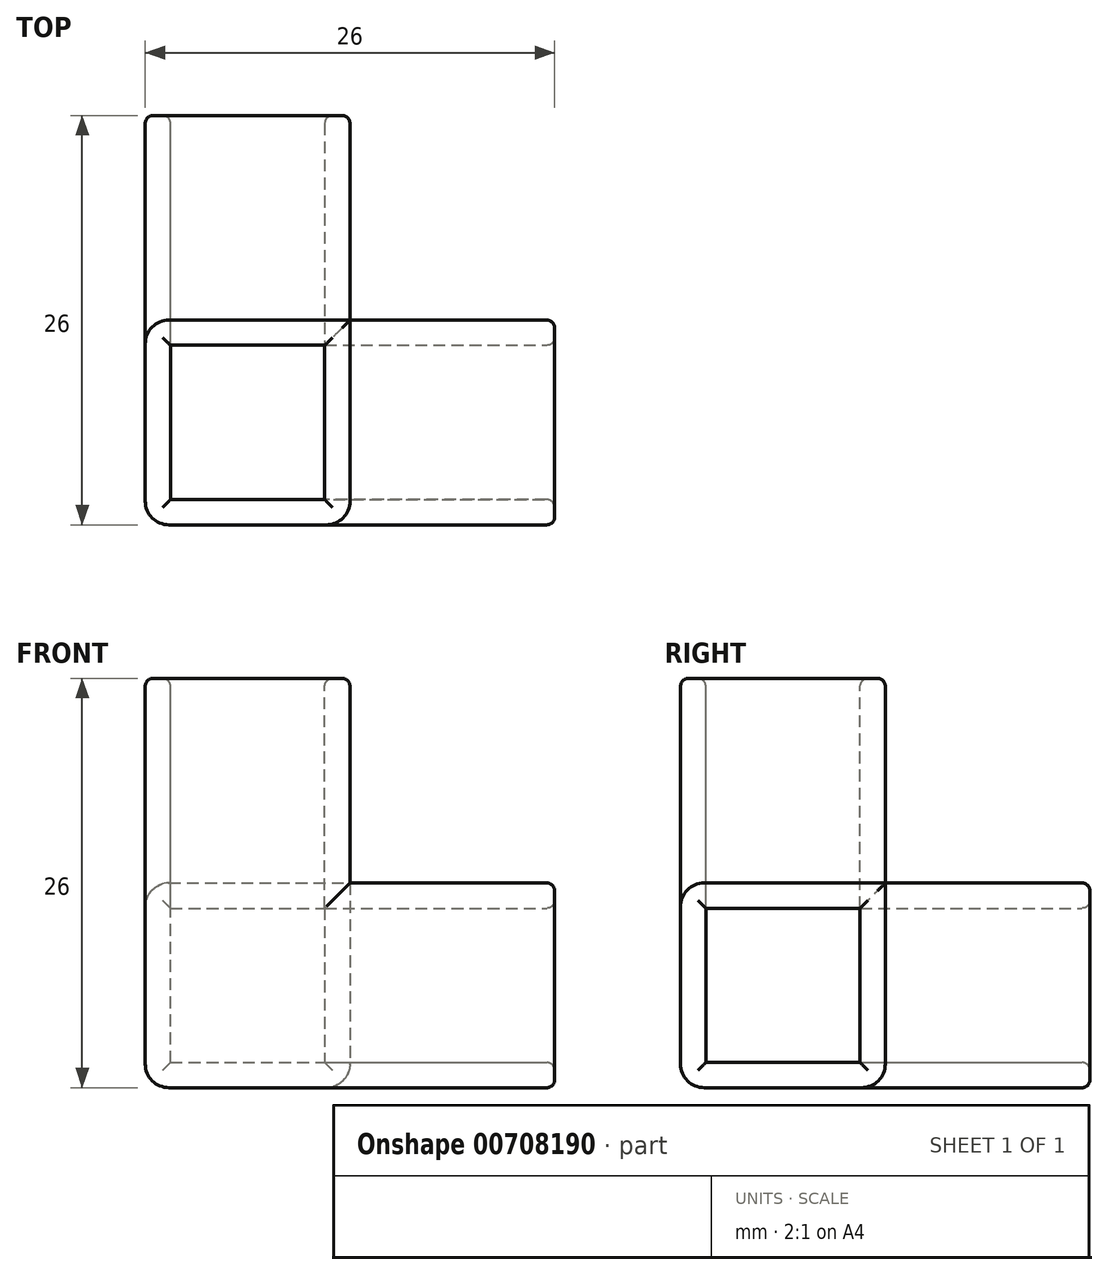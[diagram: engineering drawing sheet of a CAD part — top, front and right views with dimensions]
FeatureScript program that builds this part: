
annotation { "Feature Type Name" : "Feature", "Feature Type Description" : "" }
export const myFeature = defineFeature(function(context is Context, id is Id, definition is map)
    precondition{}
    {
        {
            var Q0;
            Q0=qCreatedBy(makeId("Top.planeOp"),FACE);
            var sketch = newSketch(context, id + "F0", { "sketchPlane" : qUnion([Q0])});
            skLineSegment(sketch, "E0", {"start": v(-6.5, 11.44) * mm, "end": v(-6.5, -1.56) * mm});
            skLineSegment(sketch, "E1", {"start": v(-6.5, -1.56) * mm, "end": v(6.5, -1.56) * mm});
            skLineSegment(sketch, "E2.0", {"start": v(-19.5, -14.56) * mm, "end": v(6.5, -14.56) * mm});
            skLineSegment(sketch, "E2.1", {"start": v(-19.5, 11.44) * mm, "end": v(-19.5, -14.56) * mm});
            skLineSegment(sketch, "E3", {"start": v(-19.5, 11.44) * mm, "end": v(-6.5, 11.44) * mm});
            skLineSegment(sketch, "E4", {"start": v(6.5, -1.56) * mm, "end": v(6.5, -14.56) * mm});
            skSolve(sketch);
        }
        {
            var Q0;
            Q0 = qSketchRegion(id + "F0", true);
            extrude(context, id + "F1", {"entities" : qUnion([Q0]), "depth" : 13 * mm, "offsetDistance" : 25 * mm});
        }
        {
            var Q0;
            Q0=makeQuery(id+"F1.opExtrude","CAP_FACE",FACE,{"disambiguationData":[OSD([sQuery(id+"F0.wireOp",EDGE,"E0"),sQuery(id+"F0.wireOp",EDGE,"E1"),sQuery(id+"F0.wireOp",EDGE,"E2.0"),sQuery(id+"F0.wireOp",EDGE,"E2.1"),sQuery(id+"F0.wireOp",EDGE,"E3"),sQuery(id+"F0.wireOp",EDGE,"E4")])],"isStart":false});
            var sketch = newSketch(context, id + "F2", { "sketchPlane" : qUnion([Q0])});
            skLineSegment(sketch, "E5", {"start": v(-6.5, -1.56) * mm, "end": v(-19.5, -1.56) * mm});
            skLineSegment(sketch, "E6", {"start": v(-19.5, -1.56) * mm, "end": v(-19.5, -14.56) * mm});
            skLineSegment(sketch, "E7", {"start": v(-19.5, -14.56) * mm, "end": v(-6.5, -14.56) * mm});
            skLineSegment(sketch, "E8", {"start": v(-6.5, -14.56) * mm, "end": v(-6.5, -1.56) * mm});
            skSolve(sketch);
        }
        {
            var Q0;
            Q0 = qSketchRegion(id + "F2", true);
            extrude(context, id + "F3", {"entities" : qUnion([Q0]), "operationType" : NewBodyOperationType.ADD, "depth" : 13 * mm, "offsetDistance" : 25 * mm});
        }
        {
            var Q0;
            Q0=makeQuery(id+"F3.opExtrude","CAP_FACE",FACE,{"disambiguationData":[OSD([sQuery(id+"F2.wireOp",EDGE,"E5"),sQuery(id+"F2.wireOp",EDGE,"E6"),sQuery(id+"F2.wireOp",EDGE,"E7"),sQuery(id+"F2.wireOp",EDGE,"E8")])],"isStart":false});
            var sketch = newSketch(context, id + "F4", { "sketchPlane" : qUnion([Q0])});
            skLineSegment(sketch, "E9.bottom", {"start": v(-17.9, -3.16) * mm, "end": v(-8.1, -3.16) * mm});
            skLineSegment(sketch, "E9.top", {"start": v(-17.9, -12.96) * mm, "end": v(-8.1, -12.96) * mm});
            skLineSegment(sketch, "E9.left", {"start": v(-17.9, -3.16) * mm, "end": v(-17.9, -12.96) * mm});
            skLineSegment(sketch, "E9.right", {"start": v(-8.1, -3.16) * mm, "end": v(-8.1, -12.96) * mm});
            skSolve(sketch);
        }
        {
            var Q0;
            Q0=makeQuery(id+"F1.opExtrude","SWEPT_FACE",FACE,{"disambiguationData":[OSD([sQuery(id+"F0.wireOp",EDGE,"E3")])]});
            var sketch = newSketch(context, id + "F5", { "sketchPlane" : qUnion([Q0])});
            skLineSegment(sketch, "E10.bottom", {"start": v(17.9, 1.6) * mm, "end": v(8.1, 1.6) * mm});
            skLineSegment(sketch, "E10.top", {"start": v(17.9, 11.4) * mm, "end": v(8.1, 11.4) * mm});
            skLineSegment(sketch, "E10.left", {"start": v(17.9, 1.6) * mm, "end": v(17.9, 11.4) * mm});
            skLineSegment(sketch, "E10.right", {"start": v(8.1, 1.6) * mm, "end": v(8.1, 11.4) * mm});
            skSolve(sketch);
        }
        {
            var Q0;
            Q0=makeQuery(id+"F1.opExtrude","CAP_EDGE",EDGE,{"disambiguationData":[OSD([sQuery(id+"F0.wireOp",EDGE,"E2.1")])],"isStart":true});
            var Q1;
            Q1=makeQuery(id+"F1.opExtrude","CAP_EDGE",EDGE,{"disambiguationData":[OSD([sQuery(id+"F0.wireOp",EDGE,"E2.0")])],"isStart":true});
            var Q2;
            Q2=makeQuery(id+"F3.boolean.opBoolean","MERGE",EDGE,{"derivedFrom":[makeQuery(id+"F1.opExtrude","SWEPT_EDGE",EDGE,{"disambiguationData":[OSD([sQuery(id+"F0.wireOp",EDGE,"E2.0"),sQuery(id+"F0.wireOp",EDGE,"E2.1")])]}),makeQuery(id+"F3.opExtrude","SWEPT_EDGE",EDGE,{"disambiguationData":[OSD([sQuery(id+"F2.wireOp",EDGE,"E6"),sQuery(id+"F2.wireOp",EDGE,"E7")])]})]});
            var Q3;
            Q3=makeQuery(id+"F3.opExtrude","SWEPT_EDGE",EDGE,{"disambiguationData":[OSD([sQuery(id+"F0.wireOp",EDGE,"E2.0"),sQuery(id+"F2.wireOp",EDGE,"E7"),sQuery(id+"F2.wireOp",EDGE,"E8")])]});
            var Q4;
            Q4=makeQuery(id+"F1.opExtrude","CAP_EDGE",EDGE,{"disambiguationData":[OSD([sQuery(id+"F0.wireOp",EDGE,"E2.0")])],"isStart":false});
            var Q5;
            Q5=makeQuery(id+"F1.opExtrude","CAP_EDGE",EDGE,{"disambiguationData":[OSD([sQuery(id+"F0.wireOp",EDGE,"E2.1")])],"isStart":false});
            var Q6;
            Q6=makeQuery(id+"F3.opExtrude","SWEPT_EDGE",EDGE,{"disambiguationData":[OSD([sQuery(id+"F0.wireOp",EDGE,"E2.1"),sQuery(id+"F2.wireOp",EDGE,"E5"),sQuery(id+"F2.wireOp",EDGE,"E6")])]});
            var Q7;
            Q7=makeQuery(id+"F1.opExtrude","CAP_EDGE",EDGE,{"disambiguationData":[OSD([sQuery(id+"F0.wireOp",EDGE,"E1")])],"isStart":true});
            var Q8;
            Q8=makeQuery(id+"F1.opExtrude","CAP_EDGE",EDGE,{"disambiguationData":[OSD([sQuery(id+"F0.wireOp",EDGE,"E0")])],"isStart":true});
            fillet(context, id + "F6", {"entities" : qUnion([Q0, Q1, Q2, Q3, Q4, Q5, Q6, Q7, Q8]), "radius" : 1.5 * mm, "tangentPropagation" : true, "allowEdgeOverflow" : false});
        }
        {
            var Q0;
            Q0=makeQuery(id+"F1.opExtrude","SWEPT_FACE",FACE,{"disambiguationData":[OSD([sQuery(id+"F0.wireOp",EDGE,"E4")])]});
            shell(context, id + "F7", {"entities" : qUnion([Q0]), "thickness" : 1.6 * mm});
        }
        {
            var Q0;
            Q0 = qSketchRegion(id + "F4", true);
            extrude(context, id + "F8", {"entities" : qUnion([Q0]), "operationType" : NewBodyOperationType.REMOVE, "oppositeDirection" : true, "depth" : 2 * mm, "offsetDistance" : 25 * mm});
        }
        {
            var Q0;
            Q0=makeQuery(id+"F5.imprint","IMPRINT",FACE,{"disambiguationData":[TD([[makeQuery(id+"F5.imprint","IMPRINT",EDGE,{"derivedFrom":sQuery(id+"F5.wireOp",EDGE,"E10.bottom")}),-1.0]])]});
            extrude(context, id + "F9", {"entities" : qUnion([Q0]), "operationType" : NewBodyOperationType.REMOVE, "oppositeDirection" : true, "depth" : 2 * mm, "offsetDistance" : 25 * mm});
        }
        {
            var Q0;
            Q0=makeQuery(id+"F1.opExtrude","SWEPT_FACE",FACE,{"disambiguationData":[OSD([sQuery(id+"F0.wireOp",EDGE,"E3")])]});
            var Q1;
            Q1=makeQuery(id+"F3.opExtrude","CAP_FACE",FACE,{"disambiguationData":[OSD([sQuery(id+"F2.wireOp",EDGE,"E5"),sQuery(id+"F2.wireOp",EDGE,"E6"),sQuery(id+"F2.wireOp",EDGE,"E7"),sQuery(id+"F2.wireOp",EDGE,"E8")])],"isStart":false});
            var Q2;
            Q2=makeQuery(id+"F1.opExtrude","SWEPT_FACE",FACE,{"disambiguationData":[OSD([sQuery(id+"F0.wireOp",EDGE,"E4")])]});
            fillet(context, id + "F10", {"entities" : qUnion([Q0, Q1, Q2]), "radius" : 0.5 * mm, "tangentPropagation" : true, "allowEdgeOverflow" : false});
        }
    });
